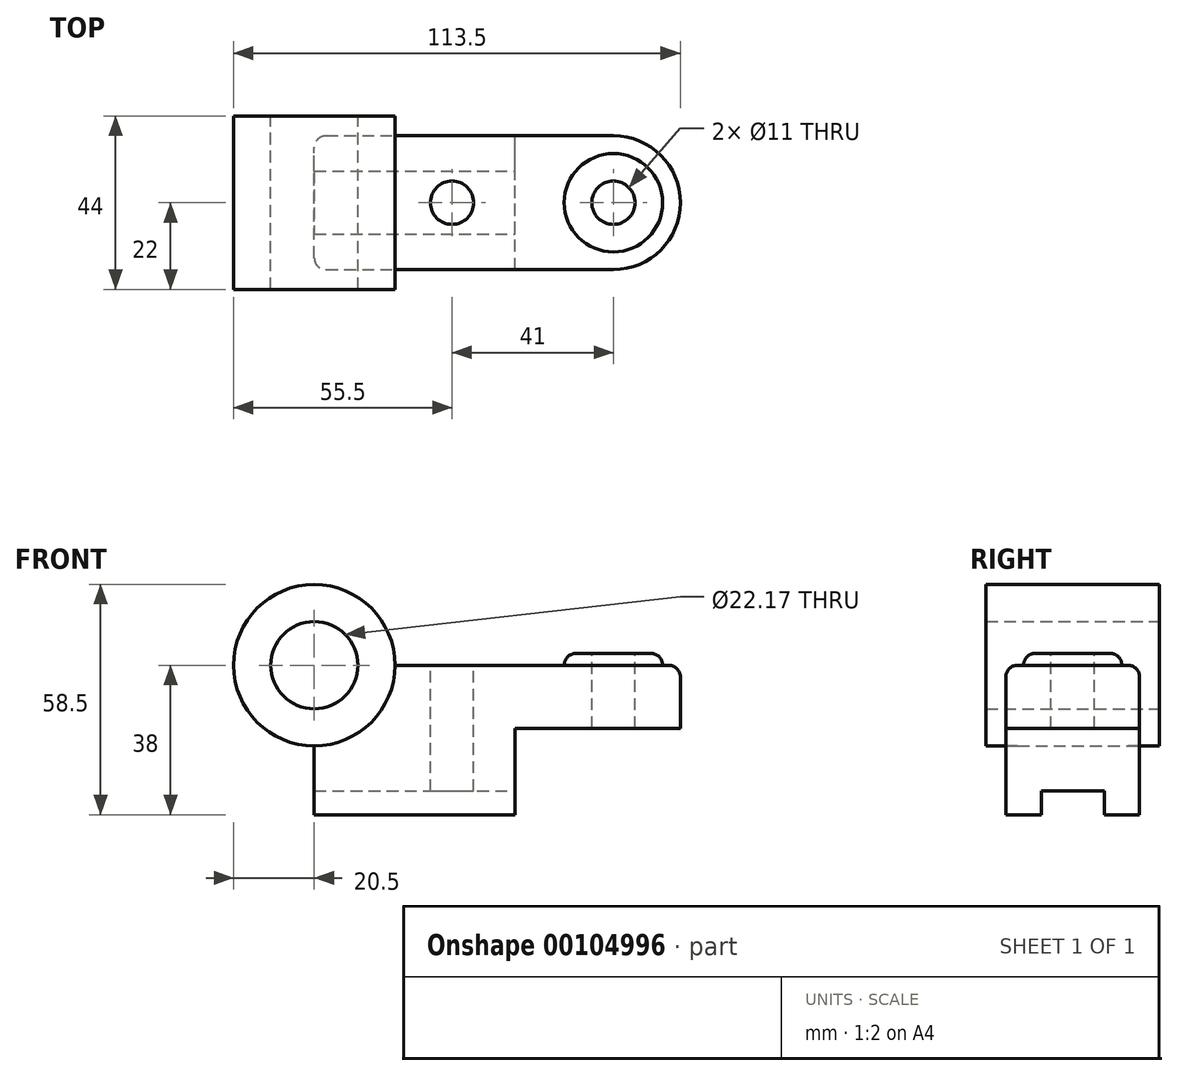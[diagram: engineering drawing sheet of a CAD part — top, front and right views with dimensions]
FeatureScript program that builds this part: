
annotation { "Feature Type Name" : "Feature", "Feature Type Description" : "" }
export const myFeature = defineFeature(function(context is Context, id is Id, definition is map)
    precondition{}
    {
        {
            var Q0;
            Q0=qCreatedBy(makeId("Front.planeOp"),FACE);
            var sketch = newSketch(context, id + "F0", { "sketchPlane" : qUnion([Q0])});
            skLineSegment(sketch, "E0.bottom", {"start": v(0, 0) * mm, "end": v(51, 0) * mm});
            skLineSegment(sketch, "E0.top", {"start": v(0, 38) * mm, "end": v(76, 38) * mm});
            skLineSegment(sketch, "E0.left", {"start": v(0, 0) * mm, "end": v(0, 38) * mm});
            skLineSegment(sketch, "E0.right", {"start": v(76, 22) * mm, "end": v(76, 38) * mm});
            skLineSegment(sketch, "E1.top", {"start": v(76, 22) * mm, "end": v(51, 22) * mm});
            skLineSegment(sketch, "E1.right", {"start": v(51, 0) * mm, "end": v(51, 22) * mm});
            skCircle(sketch, "E2", {"center": v(0, 38) * mm, "radius": 20.5 * mm});
            skCircle(sketch, "E3", {"center": v(0, 38) * mm, "radius": 11.09 * mm});
            skSolve(sketch);
        }
        {
            var Q0;
            {var subQ2=sQuery(id+"F0.wireOp",EDGE,"E0.bottom");Q0=makeQuery(id+"F0.imprint","IMPRINT",FACE,{"disambiguationData":[TD([[makeQuery(id+"F0.imprint","IMPRINT",EDGE,{"derivedFrom":subQ2}),1.0]])]});}
            extrude(context, id + "F1", {"entities" : qUnion([Q0]), "endBound" : BoundingType.SYMMETRIC, "depth" : (17 * 2) * mm});
        }
        {
            var Q0;
            {var subQ0=sQuery(id+"F0.wireOp",EDGE,"E2");var subQ1=sQuery(id+"F0.wireOp",EDGE,"E0.top");var subQ2=makeQuery(id+"F0.imprint","INTERSECT",VERTEX,{"derivedFrom":[subQ1,subQ0]});Q0=makeQuery(id+"F0.imprint","IMPRINT",FACE,{"disambiguationData":[TD([[makeQuery(id+"F0.imprint","IMPRINT",EDGE,{"disambiguationData":[TD([[subQ2,1.0]])],"derivedFrom":subQ1}),1.0]])]});}
            var Q1;
            {var subQ0=sQuery(id+"F0.wireOp",EDGE,"E2");var subQ1=sQuery(id+"F0.wireOp",EDGE,"E0.top");var subQ2=makeQuery(id+"F0.imprint","INTERSECT",VERTEX,{"derivedFrom":[subQ1,subQ0]});Q1=makeQuery(id+"F0.imprint","IMPRINT",FACE,{"disambiguationData":[TD([[makeQuery(id+"F0.imprint","IMPRINT",EDGE,{"disambiguationData":[TD([[subQ2,1.0]])],"derivedFrom":subQ1}),-1.0]])]});}
            extrude(context, id + "F2", {"entities" : qUnion([Q0, Q1]), "operationType" : NewBodyOperationType.ADD, "endBound" : BoundingType.SYMMETRIC, "depth" : 44 * mm});
        }
        {
            var Q0;
            Q0=makeQuery(id+"F1.opExtrude","SWEPT_FACE",FACE,{"disambiguationData":[OSD([sQuery(id+"F0.wireOp",EDGE,"E0.top")])]});
            var sketch = newSketch(context, id + "F3", { "sketchPlane" : qUnion([Q0])});
            skArc(sketch, "E4", {"start": v(76, -17) * mm, "mid": v(93, 0) * mm, "end": v(76, 17) * mm});
            skSolve(sketch);
        }
        {
            var Q0;
            Q0=makeQuery(id+"F3.imprint","IMPRINT",FACE,{"disambiguationData":[TD([[makeQuery(id+"F3.imprint","IMPRINT",EDGE,{"derivedFrom":sQuery(id+"F3.wireOp",EDGE,"E4")}),1.0]])]});
            var Q1;
            Q1=makeQuery(id+"F1.opExtrude","SWEPT_FACE",FACE,{"disambiguationData":[OSD([sQuery(id+"F0.wireOp",EDGE,"E1.top")])]});
            extrude(context, id + "F4", {"entities" : qUnion([Q0]), "operationType" : NewBodyOperationType.ADD, "endBound" : BoundingType.UP_TO_SURFACE, "oppositeDirection" : true, "endBoundEntityFace" : qUnion([Q1]), "depth" : 25 * mm});
        }
        {
            var Q0;
            {var subQ0=sQuery(id+"F0.wireOp",EDGE,"E0.top");Q0=makeQuery(id+"F4.boolean.opBoolean","MERGE",FACE,{"derivedFrom":[makeQuery(id+"F1.opExtrude","SWEPT_FACE",FACE,{"disambiguationData":[OSD([subQ0])]}),makeQuery(id+"F4.opExtrude","CAP_FACE",FACE,{"disambiguationData":[OSD([subQ0,sQuery(id+"F0.wireOp",EDGE,"E0.right"),sQuery(id+"F3.wireOp",EDGE,"E4")])],"isStart":true})]});}
            var sketch = newSketch(context, id + "F5", { "sketchPlane" : qUnion([Q0])});
            skCircle(sketch, "E5", {"center": v(76, 0) * mm, "radius": 12.5 * mm});
            skSolve(sketch);
        }
        {
            var Q0;
            Q0=makeQuery(id+"F5.imprint","IMPRINT",FACE,{"disambiguationData":[TD([[makeQuery(id+"F5.imprint","IMPRINT",EDGE,{"derivedFrom":sQuery(id+"F5.wireOp",EDGE,"E5")}),1.0]])]});
            extrude(context, id + "F6", {"entities" : qUnion([Q0]), "operationType" : NewBodyOperationType.ADD, "depth" : 3 * mm});
        }
        {
            var Q0;
            Q0=makeQuery(id+"F6.opExtrude","CAP_FACE",FACE,{"disambiguationData":[OSD([sQuery(id+"F5.wireOp",EDGE,"E5")])],"isStart":false});
            var sketch = newSketch(context, id + "F7", { "sketchPlane" : qUnion([Q0])});
            skCircle(sketch, "E6", {"center": v(76, 0) * mm, "radius": 5.5 * mm});
            skCircle(sketch, "E7", {"center": v(35, 0) * mm, "radius": 5.5 * mm});
            skSolve(sketch);
        }
        {
            var Q0;
            Q0 = qSketchRegion(id + "F7", true);
            extrude(context, id + "F8", {"entities" : qUnion([Q0]), "operationType" : NewBodyOperationType.REMOVE, "endBound" : BoundingType.THROUGH_ALL, "oppositeDirection" : true, "depth" : 25 * mm});
        }
        {
            var Q0;
            Q0=makeQuery(id+"F1.opExtrude","SWEPT_FACE",FACE,{"disambiguationData":[OSD([sQuery(id+"F0.wireOp",EDGE,"E1.right")])]});
            var sketch = newSketch(context, id + "F9", { "sketchPlane" : qUnion([Q0])});
            skLineSegment(sketch, "E8.bottom", {"start": v(-8, 0) * mm, "end": v(8, 0) * mm});
            skLineSegment(sketch, "E8.top", {"start": v(-8, 6) * mm, "end": v(8, 6) * mm});
            skLineSegment(sketch, "E8.left", {"start": v(-8, 0) * mm, "end": v(-8, 6) * mm});
            skLineSegment(sketch, "E8.right", {"start": v(8, 0) * mm, "end": v(8, 6) * mm});
            skSolve(sketch);
        }
        {
            var Q0;
            Q0=makeQuery(id+"F9.imprint","IMPRINT",FACE,{"disambiguationData":[TD([[makeQuery(id+"F9.imprint","IMPRINT",EDGE,{"derivedFrom":sQuery(id+"F9.wireOp",EDGE,"E8.bottom")}),1.0]])]});
            extrude(context, id + "F10", {"entities" : qUnion([Q0]), "operationType" : NewBodyOperationType.REMOVE, "endBound" : BoundingType.THROUGH_ALL, "oppositeDirection" : true, "depth" : 25 * mm});
        }
        {
            var Q0;
            Q0=makeQuery(id+"F1.opExtrude","SWEPT_EDGE",EDGE,{"disambiguationData":[OSD([sQuery(id+"F0.wireOp",EDGE,"E0.top"),sQuery(id+"F0.wireOp",EDGE,"E2")])]});
            var Q1;
            Q1=makeQuery(id+"F1.opExtrude","CAP_EDGE",EDGE,{"disambiguationData":[OSD([sQuery(id+"F0.wireOp",EDGE,"E0.top")])],"isStart":false});
            var Q2;
            Q2=makeQuery(id+"F1.opExtrude","SWEPT_EDGE",EDGE,{"disambiguationData":[OSD([sQuery(id+"F0.wireOp",EDGE,"E0.left"),sQuery(id+"F0.wireOp",EDGE,"E2")])]});
            var Q3;
            Q3=makeQuery(id+"F1.opExtrude","CAP_EDGE",EDGE,{"disambiguationData":[OSD([sQuery(id+"F0.wireOp",EDGE,"E0.left")])],"isStart":true});
            var Q4;
            Q4=makeQuery(id+"F1.opExtrude","CAP_EDGE",EDGE,{"disambiguationData":[OSD([sQuery(id+"F0.wireOp",EDGE,"E0.left")])],"isStart":false});
            fillet(context, id + "F11", {"entities" : qUnion([Q0, Q1, Q2, Q3, Q4]), "radius" : 3 * mm, "tangentPropagation" : true, "allowEdgeOverflow" : false});
        }
        {
            var Q0;
            Q0=makeQuery(id+"F6.opExtrude","CAP_EDGE",EDGE,{"disambiguationData":[OSD([sQuery(id+"F5.wireOp",EDGE,"E5")])],"isStart":false});
            fillet(context, id + "F12", {"entities" : qUnion([Q0]), "radius" : 3 * mm, "tangentPropagation" : true, "allowEdgeOverflow" : false});
        }
    });
